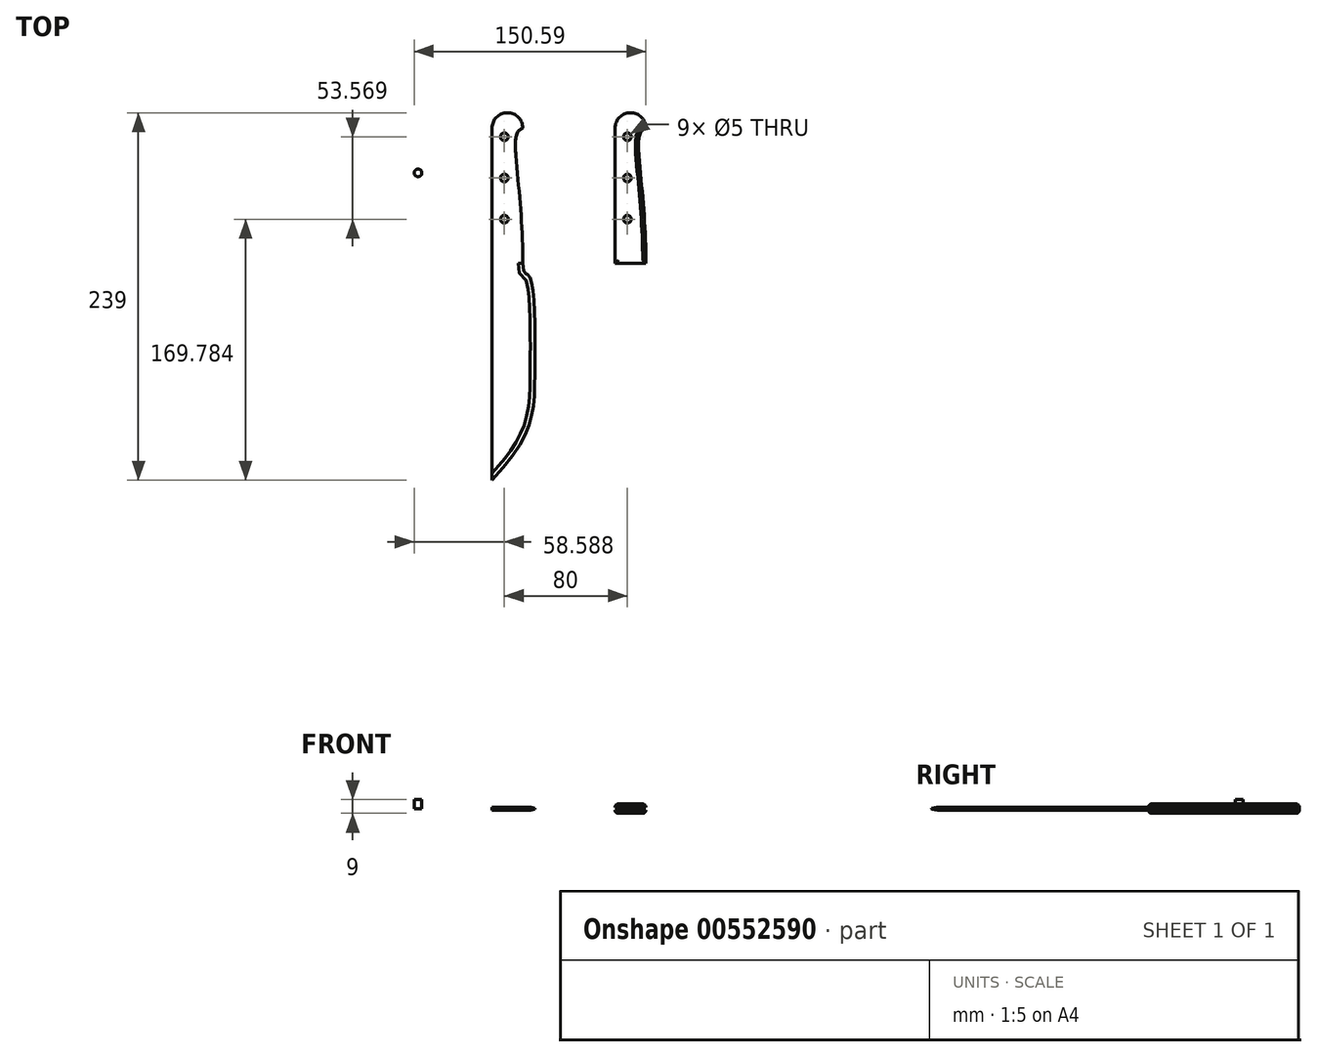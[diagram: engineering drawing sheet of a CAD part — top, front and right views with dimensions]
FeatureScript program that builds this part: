
annotation { "Feature Type Name" : "Feature", "Feature Type Description" : "" }
export const myFeature = defineFeature(function(context is Context, id is Id, definition is map)
    precondition{}
    {
        {
            var Q0;
            Q0=qCreatedBy(makeId("Front.planeOp"),FACE);
            cPlane(context, id + "F0", {"entities" : qUnion([Q0]), "cplaneType" : CPlaneType.OFFSET, "offset" : 100 * mm, "oppositeDirection" : true, "width" : 150 * mm, "height" : 150 * mm});
        }
        {
            var Q0;
            Q0=qCreatedBy(id+"F0.planeOp",FACE);
            var sketch = newSketch(context, id + "F1", { "sketchPlane" : qUnion([Q0])});
            skLineSegment(sketch, "E0.bottom", {"start": v(10.5, 3) * mm, "end": v(-10.5, 3) * mm});
            skLineSegment(sketch, "E0.top", {"start": v(10.5, -3) * mm, "end": v(-10.5, -3) * mm});
            skLineSegment(sketch, "E0.left", {"start": v(10.5, 3) * mm, "end": v(10.5, -3) * mm});
            skLineSegment(sketch, "E0.right", {"start": v(-10.5, 3) * mm, "end": v(-10.5, -3) * mm});
            skPoint(sketch, "E0.middle", {"position": v(0, 0) * mm});
            skSolve(sketch);
        }
        {
            var Q0;
            Q0=makeQuery(id+"F1.imprint","IMPRINT",FACE,{"disambiguationData":[TD([[makeQuery(id+"F1.imprint","IMPRINT",EDGE,{"derivedFrom":sQuery(id+"F1.wireOp",EDGE,"E0.bottom")}),1.0]])]});
            var Q1;
            Q1=qCreatedBy(makeId("Front.planeOp"),FACE);
            extrude(context, id + "F2", {"entities" : qUnion([Q0]), "endBound" : BoundingType.UP_TO_SURFACE, "depth" : 25 * mm, "endBoundEntityFace" : qUnion([Q1]), "offsetDistance" : 25 * mm});
        }
        {
            var Q0;
            Q0=qCreatedBy(makeId("Top.planeOp"),FACE);
            var sketch = newSketch(context, id + "F3", { "sketchPlane" : qUnion([Q0])});
            skLineSegment(sketch, "E1", {"start": v(0, 0) * mm, "end": v(0, -141) * mm, "construction": true});
            skLineSegment(sketch, "E2", {"start": v(0, 0) * mm, "end": v(-10, 0) * mm, "construction": true});
            skLineSegment(sketch, "E3", {"start": v(0, 0) * mm, "end": v(10, 0) * mm, "construction": true});
            skLineSegment(sketch, "E4", {"start": v(-10, 0) * mm, "end": v(-10, -141) * mm});
            skLineSegment(sketch, "E5", {"start": v(0, -70.5) * mm, "end": v(17.8, -70.5) * mm, "construction": true});
            skLineSegment(sketch, "E6", {"start": v(0, -8) * mm, "end": v(14, -8) * mm, "construction": true});
            skFitSpline(sketch, "E7", {"points": [v(-10, -141) * mm, v(17.8, -70.5) * mm, v(14, -8) * mm, v(10, 0) * mm], "startDerivative": vector(187.86, 202.73) * mm, "endDerivative": vector(0, 157.36) * mm});
            skLineSegment(sketch, "E8", {"start": v(10, 0) * mm, "end": v(10, -8) * mm, "construction": true});
            skLineSegment(sketch, "E9", {"start": v(10, 0) * mm, "end": v(-10, 0) * mm});
            skSolve(sketch);
        }
        {
            var Q0;
            Q0=makeQuery(id+"F3.imprint","IMPRINT",FACE,{"disambiguationData":[TD([[makeQuery(id+"F3.imprint","IMPRINT",EDGE,{"derivedFrom":sQuery(id+"F3.wireOp",EDGE,"E4")}),1.0]])]});
            extrude(context, id + "F4", {"entities" : qUnion([Q0]), "operationType" : NewBodyOperationType.ADD, "depth" : 2 * mm, "offsetDistance" : 25 * mm, "symmetric" : true});
        }
        {
            var Q0;
            Q0=qCreatedBy(makeId("Front.planeOp"),FACE);
            cPlane(context, id + "F5", {"entities" : qUnion([Q0]), "cplaneType" : CPlaneType.OFFSET, "offset" : 141 * mm, "width" : 150 * mm, "height" : 150 * mm});
        }
        {
            var Q0;
            Q0=makeQuery(id+"F4.opExtrude","CAP_EDGE",EDGE,{"disambiguationData":[OSD([sQuery(id+"F3.wireOp",EDGE,"E7")])],"isStart":false});
            var Q1;
            Q1=makeQuery(id+"F4.opExtrude","CAP_EDGE",EDGE,{"disambiguationData":[OSD([sQuery(id+"F3.wireOp",EDGE,"E7")])],"isStart":true});
            chamfer(context, id + "F6", {"entities" : qUnion([Q0, Q1]), "chamferType" : ChamferType.TWO_OFFSETS, "width1" : 3 * mm, "oppositeDirection" : false, "width2" : 0.8 * mm, "tangentPropagation" : true});
        }
        {
            var Q0;
            Q0=makeQuery(id+"F2.opExtrude","SWEPT_FACE",FACE,{"disambiguationData":[OSD([sQuery(id+"F1.wireOp",EDGE,"E0.bottom")])]});
            cPlane(context, id + "F7", {"entities" : qUnion([Q0]), "cplaneType" : CPlaneType.OFFSET, "offset" : 25 * mm, "width" : 150 * mm, "height" : 150 * mm});
        }
        {
            var Q0;
            Q0=qCreatedBy(id+"F7.planeOp",FACE);
            var sketch = newSketch(context, id + "F8", { "sketchPlane" : qUnion([Q0])});
            skLineSegment(sketch, "E10", {"start": v(0, 0) * mm, "end": v(-10, 0) * mm, "construction": true});
            skLineSegment(sketch, "E11", {"start": v(0, 0) * mm, "end": v(10, 0) * mm, "construction": true});
            skLineSegment(sketch, "E12", {"start": v(-10, 0) * mm, "end": v(-10, 88) * mm});
            skLineSegment(sketch, "E13", {"start": v(10, 0) * mm, "end": v(10, 88) * mm, "construction": true});
            skArc(sketch, "E14", {"start": v(10, 88) * mm, "mid": v(0, 98) * mm, "end": v(-10, 88) * mm});
            skLineSegment(sketch, "E15", {"start": v(10, 88) * mm, "end": v(6, 88) * mm, "construction": true});
            skLineSegment(sketch, "E16", {"start": v(6, 88) * mm, "end": v(6, 84) * mm, "construction": true});
            skFitSpline(sketch, "E17", {"points": [v(10, 88) * mm, v(6, 84) * mm, v(10, 0) * mm], "startDerivative": vector(-25.37, -12.54) * mm, "endDerivative": vector(0, -166.24) * mm});
            skLineSegment(sketch, "E18.bottom", {"start": v(-57.94, 120.24) * mm, "end": v(54.48, 120.24) * mm});
            skLineSegment(sketch, "E18.left", {"start": v(-57.94, 120.24) * mm, "end": v(-57.94, 0) * mm});
            skLineSegment(sketch, "E18.right", {"start": v(54.48, 120.24) * mm, "end": v(54.48, 0) * mm});
            skLineSegment(sketch, "E19", {"start": v(10, 0) * mm, "end": v(54.48, 0) * mm});
            skLineSegment(sketch, "E20", {"start": v(-10, 0) * mm, "end": v(-57.94, 0) * mm});
            skSolve(sketch);
        }
        {
            var Q0;
            Q0=makeQuery(id+"F8.imprint","IMPRINT",FACE,{"disambiguationData":[TD([[makeQuery(id+"F8.imprint","IMPRINT",EDGE,{"derivedFrom":sQuery(id+"F8.wireOp",EDGE,"E12")}),1.0]])]});
            extrude(context, id + "F9", {"entities" : qUnion([Q0]), "operationType" : NewBodyOperationType.REMOVE, "endBound" : BoundingType.THROUGH_ALL, "oppositeDirection" : true, "depth" : 25 * mm, "offsetDistance" : 25 * mm});
        }
        {
            var Q0;
            Q0=makeQuery(id+"F2.opExtrude","SWEPT_FACE",FACE,{"disambiguationData":[OSD([sQuery(id+"F1.wireOp",EDGE,"E0.bottom")])]});
            var Q1;
            Q1=makeQuery(id+"F2.opExtrude","SWEPT_FACE",FACE,{"disambiguationData":[OSD([sQuery(id+"F1.wireOp",EDGE,"E0.top")])]});
            fillet(context, id + "F10", {"entities" : qUnion([Q0, Q1]), "radius" : 2 * mm, "tangentPropagation" : true, "allowEdgeOverflow" : false});
        }
        {
            var Q0;
            Q0=qCreatedBy(id+"F5.planeOp",FACE);
            var sketch = newSketch(context, id + "F11", { "sketchPlane" : qUnion([Q0])});
            skLineSegment(sketch, "E21.bottom", {"start": v(25, 1) * mm, "end": v(-25, 1) * mm});
            skLineSegment(sketch, "E21.top", {"start": v(25, -1) * mm, "end": v(-25, -1) * mm});
            skLineSegment(sketch, "E21.left", {"start": v(25, 1) * mm, "end": v(25, -1) * mm});
            skLineSegment(sketch, "E21.right", {"start": v(-25, 1) * mm, "end": v(-25, -1) * mm});
            skPoint(sketch, "E21.middle", {"position": v(0, 0) * mm});
            skLineSegment(sketch, "E22.bottom", {"start": v(-35.18, 21.9) * mm, "end": v(44.5, 21.9) * mm});
            skLineSegment(sketch, "E22.top", {"start": v(-35.18, -25.46) * mm, "end": v(44.5, -25.46) * mm});
            skLineSegment(sketch, "E22.left", {"start": v(-35.18, 21.9) * mm, "end": v(-35.18, -25.46) * mm});
            skLineSegment(sketch, "E22.right", {"start": v(44.5, 21.9) * mm, "end": v(44.5, -25.46) * mm});
            skSolve(sketch);
        }
        {
            var Q0;
            Q0=makeQuery(id+"F2.opExtrude","SWEPT_FACE",FACE,{"disambiguationData":[OSD([sQuery(id+"F1.wireOp",EDGE,"E0.bottom")])]});
            var sketch = newSketch(context, id + "F12", { "sketchPlane" : qUnion([Q0])});
            skLineSegment(sketch, "E23", {"start": v(-8, 2) * mm, "end": v(4, 2) * mm, "construction": true});
            skLineSegment(sketch, "E24", {"start": v(-2, 2) * mm, "end": v(-2, 95.75) * mm, "construction": true});
            skCircle(sketch, "E25", {"center": v(-2, 28.78) * mm, "radius": 2.5 * mm});
            skCircle(sketch, "E26", {"center": v(-2, 55.57) * mm, "radius": 2.5 * mm});
            skCircle(sketch, "E27", {"center": v(-2, 82.35) * mm, "radius": 2.5 * mm});
            skSolve(sketch);
        }
        {
            var Q0;
            Q0=makeQuery(id+"F12.imprint","IMPRINT",FACE,{"disambiguationData":[TD([[makeQuery(id+"F12.imprint","IMPRINT",EDGE,{"derivedFrom":sQuery(id+"F12.wireOp",EDGE,"E27")}),1.0]])]});
            var Q1;
            Q1=makeQuery(id+"F12.imprint","IMPRINT",FACE,{"disambiguationData":[TD([[makeQuery(id+"F12.imprint","IMPRINT",EDGE,{"derivedFrom":sQuery(id+"F12.wireOp",EDGE,"E26")}),1.0]])]});
            var Q2;
            Q2=makeQuery(id+"F12.imprint","IMPRINT",FACE,{"disambiguationData":[TD([[makeQuery(id+"F12.imprint","IMPRINT",EDGE,{"derivedFrom":sQuery(id+"F12.wireOp",EDGE,"E25")}),1.0]])]});
            extrude(context, id + "F13", {"entities" : qUnion([Q0, Q1, Q2]), "operationType" : NewBodyOperationType.REMOVE, "endBound" : BoundingType.THROUGH_ALL, "oppositeDirection" : true, "depth" : 25 * mm, "offsetDistance" : 25 * mm});
        }
        {
            var Q0;
            Q0=makeQuery(id+"F2.opExtrude","SWEPT_BODY",BODY,{"disambiguationData":[OSD([sQuery(id+"F1.wireOp",EDGE,"E0.bottom"),sQuery(id+"F1.wireOp",EDGE,"E0.top"),sQuery(id+"F1.wireOp",EDGE,"E0.left"),sQuery(id+"F1.wireOp",EDGE,"E0.right")])]});
            transform(context, id + "F14", {"entities" : qUnion([Q0]), "transformType" : TransformType.TRANSLATION_3D, "dx" : 80 * mm, "dy" : 0 * mm, "dz" : 0 * mm, "makeCopy" : true});
        }
        {
            var Q0;
            Q0=makeQuery(id+"F11.imprint","IMPRINT",FACE,{"disambiguationData":[TD([[makeQuery(id+"F11.imprint","IMPRINT",EDGE,{"derivedFrom":sQuery(id+"F11.wireOp",EDGE,"E21.bottom")}),-1.0]])]});
            extrude(context, id + "F15", {"entities" : qUnion([Q0]), "operationType" : NewBodyOperationType.REMOVE, "endBound" : BoundingType.THROUGH_ALL, "oppositeDirection" : true, "depth" : 25 * mm, "offsetDistance" : 25 * mm});
        }
        {
            var Q0;
            Q0=qCreatedBy(id+"F5.planeOp",FACE);
            var sketch = newSketch(context, id + "F16", { "sketchPlane" : qUnion([Q0])});
            skLineSegment(sketch, "E28.bottom", {"start": v(101.81, 1) * mm, "end": v(58.19, 1) * mm});
            skLineSegment(sketch, "E28.top", {"start": v(101.81, -1) * mm, "end": v(58.19, -1) * mm});
            skLineSegment(sketch, "E28.left", {"start": v(101.81, 1) * mm, "end": v(101.81, -1) * mm});
            skLineSegment(sketch, "E28.right", {"start": v(58.19, 1) * mm, "end": v(58.19, -1) * mm});
            skPoint(sketch, "E28.middle", {"position": v(80, 0) * mm});
            skSolve(sketch);
        }
        {
            var Q0;
            Q0=makeQuery(id+"F16.imprint","IMPRINT",FACE,{"disambiguationData":[TD([[makeQuery(id+"F16.imprint","IMPRINT",EDGE,{"derivedFrom":sQuery(id+"F16.wireOp",EDGE,"E28.bottom")}),1.0]])]});
            extrude(context, id + "F17", {"entities" : qUnion([Q0]), "operationType" : NewBodyOperationType.REMOVE, "endBound" : BoundingType.THROUGH_ALL, "oppositeDirection" : true, "depth" : 25 * mm, "offsetDistance" : 25 * mm});
        }
        {
            var Q0;
            Q0=qCreatedBy(makeId("Top.planeOp"),FACE);
            var sketch = newSketch(context, id + "F18", { "sketchPlane" : qUnion([Q0])});
            skCircle(sketch, "E29", {"center": v(-58.09, 58.89) * mm, "radius": 2.5 * mm});
            skSolve(sketch);
        }
        {
            var Q0;
            Q0=makeQuery(id+"F18.imprint","IMPRINT",FACE,{"disambiguationData":[TD([[makeQuery(id+"F18.imprint","IMPRINT",EDGE,{"derivedFrom":sQuery(id+"F18.wireOp",EDGE,"E29")}),1.0]])]});
            extrude(context, id + "F19", {"entities" : qUnion([Q0]), "depth" : 6 * mm, "offsetDistance" : 25 * mm});
        }
    });
